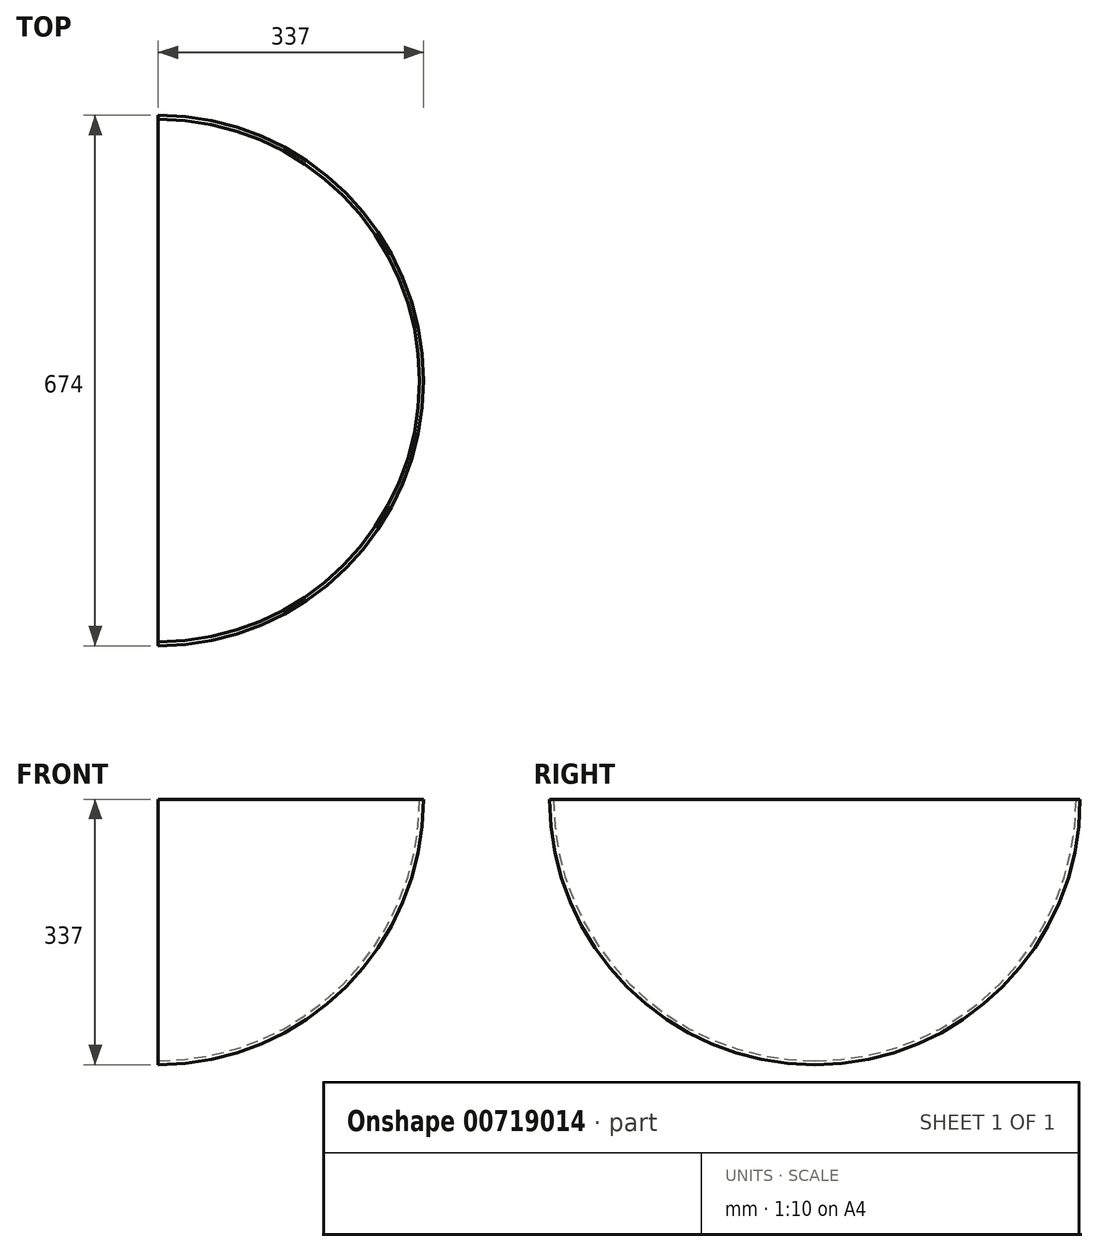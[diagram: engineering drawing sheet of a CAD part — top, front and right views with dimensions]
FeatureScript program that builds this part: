
annotation { "Feature Type Name" : "Feature", "Feature Type Description" : "" }
export const myFeature = defineFeature(function(context is Context, id is Id, definition is map)
    precondition{}
    {
        {
            var Q0;
            Q0=qCreatedBy(makeId("Front.planeOp"),FACE);
            var sketch = newSketch(context, id + "F0", { "sketchPlane" : qUnion([Q0])});
            skArc(sketch, "E0.0", {"start": v(0, -332) * mm, "mid": v(234.76, -234.76) * mm, "end": v(332, 0) * mm});
            skArc(sketch, "E1.0", {"start": v(0, -337) * mm, "mid": v(238.3, -238.3) * mm, "end": v(337, 0) * mm});
            skLineSegment(sketch, "E2.0", {"start": v(0, 0) * mm, "end": v(337, 0) * mm, "construction": true});
            skLineSegment(sketch, "E3", {"start": v(332, 0) * mm, "end": v(337, 0) * mm});
            skLineSegment(sketch, "E4", {"start": v(0, -332) * mm, "end": v(0, -337) * mm});
            skLineSegment(sketch, "E5", {"start": v(0, 0) * mm, "end": v(0, -332) * mm, "construction": true});
            skSolve(sketch);
        }
        {
            var Q0;
            Q0 = qSketchRegion(id + "F0", true);
            var Q1;
            Q1=sQuery(id+"F0.wireOp",EDGE,"E5");
            revolve(context, id + "F1", {"surfaceOperationType" : NewSurfaceOperationType.NEW, "entities" : qUnion([Q0]), "axis" : qUnion([Q1]), "revolveType" : RevolveType.SYMMETRIC, "angle" : 180 * degree});
        }
    });
